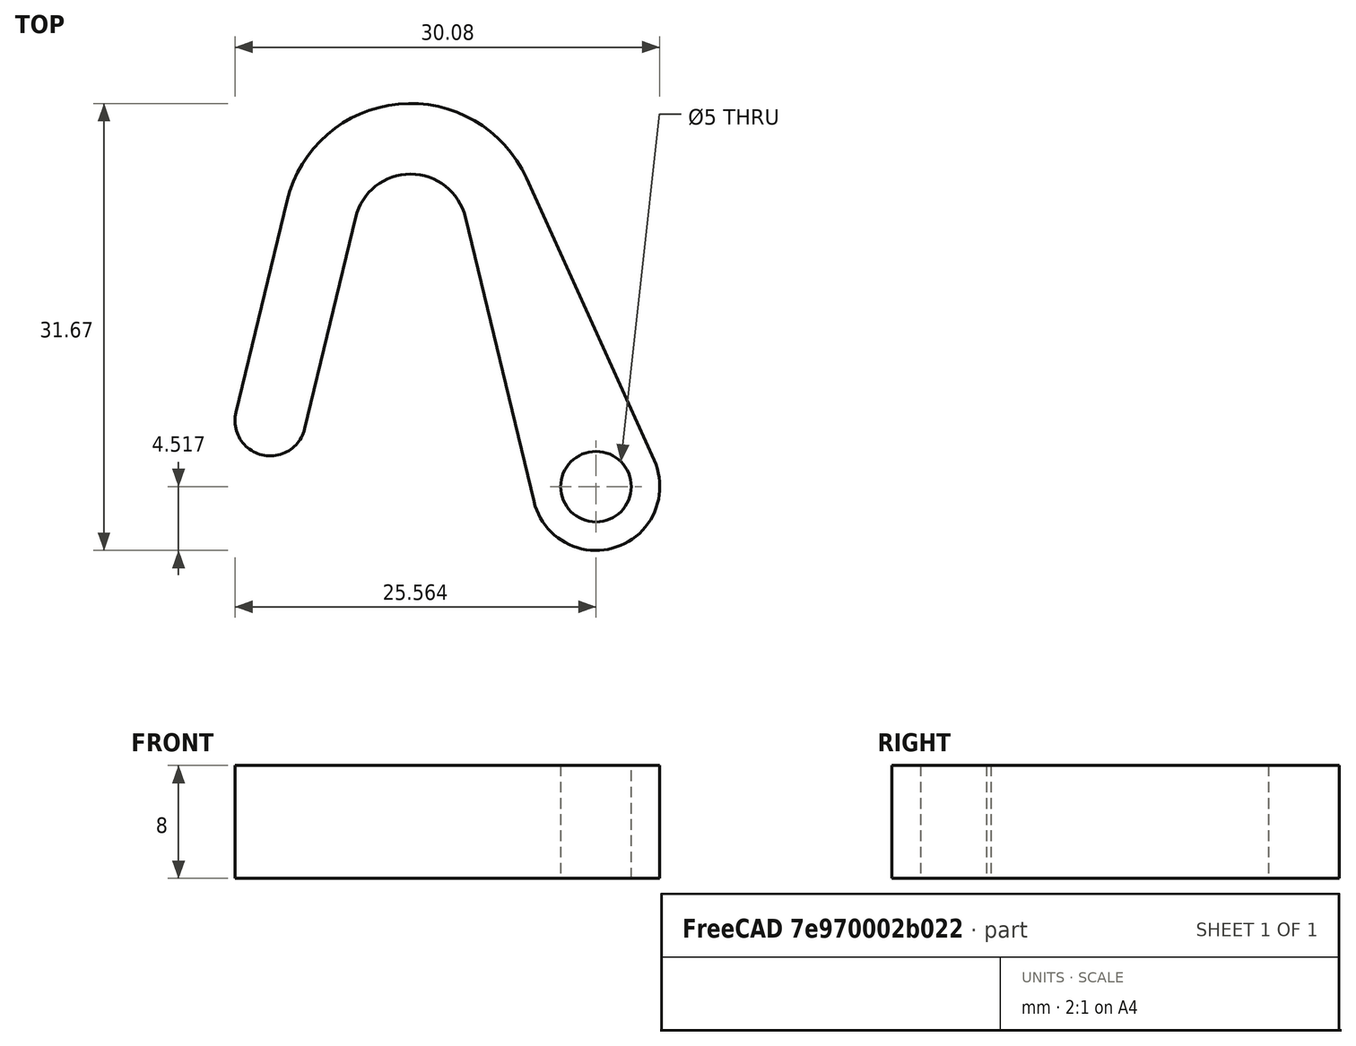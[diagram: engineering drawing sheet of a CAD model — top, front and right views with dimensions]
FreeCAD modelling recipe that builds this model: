
FCSTD DOCUMENT  (FreeCAD 1.0R39285 (Git))
Label: fox bowl hook
License: All rights reserved
LicenseURL: https://en.wikipedia.org/wiki/All_rights_reserved
objects: Sketcher::SketchObject×1, PartDesign::Pad×1, PartDesign::Body×1
note: 6 computed .brp shape members not serialized (recipe doc carries the construction recipe); baked Part::Feature solids carry a one-line shape summary decoded from their .brp

FEATURE [Sketcher::SketchObject] Sketch
  ArcFitTolerance = 1e-06
  AttachmentSupport = -> [XY_Plane]
  FullyConstrained = true
  MakeInternals = false
  MapMode = 5
  sketch-geometry (13):
    g0: LineSegment StartX=-7.5 StartY=-18.0638 StartZ=0 EndX=-3.88889 EndY=-3.06379 EndZ=0
    g1: LineSegment StartX=3.88889 StartY=-3.06379 StartZ=0 EndX=8.73907 EndY=-23.2107 EndZ=0
    g2: LineSegment StartX=17.2516 StartY=-20.2889 StartZ=0 EndX=8.19924 EndY=-0.288881 EndZ=0
    g3: LineSegment StartX=-8.75001 StartY=-1.89352 StartZ=0 EndX=-12.3611 EndY=-16.8935 EndZ=0
    g4: ArcOfCircle CenterX=-2e-16 CenterY=-4 CenterZ=0 NormalX=0 NormalY=0 NormalZ=1 AngleXU=0 Radius=9 StartAngle=0.425028 EndAngle=2.90535
    g5: Circle CenterX=13.1336 CenterY=-22.1527 CenterZ=0 NormalX=0 NormalY=0 NormalZ=1 AngleXU=0 Radius=2.5
    g6: ArcOfCircle CenterX=-9.93056 CenterY=-17.4787 CenterZ=0 NormalX=0 NormalY=0 NormalZ=1 AngleXU=0 Radius=2.5 StartAngle=2.90535 EndAngle=6.04694
    g7: ArcOfCircle CenterX=13.1336 CenterY=-22.1527 CenterZ=0 NormalX=0 NormalY=0 NormalZ=1 AngleXU=0 Radius=4.52012 StartAngle=3.37784 EndAngle=6.70821
    g8: ArcOfCircle CenterX=-2e-16 CenterY=-4 CenterZ=0 NormalX=0 NormalY=0 NormalZ=1 AngleXU=0 Radius=4 StartAngle=0.236245 EndAngle=2.90535
    g9: GeomPoint [constr] X=0 Y=0 Z=0
    g10: GeomPoint [constr] X=0 Y=0 Z=0
    g11: GeomPoint [constr] X=0 Y=0 Z=0
    g12: GeomPoint [constr] X=7.5 Y=-18.0638 Z=0
  constraints (25):
    c: Tangent(g3,g4) = -1.5708
    c: Tangent(g6,g0) = -1.5708
    c: Tangent(g6,g3) = -1.5708
    c: Tangent(g8,g0) = 1.5708
    c: Tangent(g7,g1) = -1.5708
    c: Tangent(g7,g2) = -1.5708
    c: Coincident(g5,g7)
    c: Coincident(g4,g8)
    c: Distance(g0,g3) = 5
    c: Coincident(g9,g-1)
    c: Tangent(g4,g2) = -1.5708
    c: Symmetric(g1,g0,g-2)
    c: Coincident(g8,g1)
    c: Coincident(g10,g9)
    c: PointOnObject(g11,g8)
    c: Coincident(g11,g9)
    c: Diameter(g8) = 8
    c: Parallel(g0,g3)
    c: Diameter(g5) = 5
    c: DistanceY(g0,g0) = 15
    c: PointOnObject(g12,g1)
    c: Symmetric(g12,g0,g-2)
    c: DistanceX(g0,g12) = 15
    c: DistanceY(g2,g2) = 20
    c: Distance(g1,g2) = 9
FEATURE [PartDesign::Pad] Pad
  Direction = (0,0,1)
  Length = 8
  Length2 = 10
  Profile = -> Sketch
  ReferenceAxis = -> Sketch [N_Axis]
  Refine = true
  Suppressed = false
  Type = 0
FEATURE [PartDesign::Body] Body
  AllowCompound = false
  Group = -> [Sketch,Pad]
  Origin = -> Origin
  Tip = -> Pad
